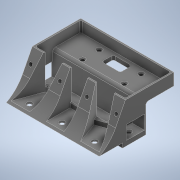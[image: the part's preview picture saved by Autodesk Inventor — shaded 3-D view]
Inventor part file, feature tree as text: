
AUTODESK INVENTOR PART (.ipt)
format: ipt  version: 2021 (Build 250183000, 183)  size: 572,928 bytes
history: native  units: mm
features: other x21, sketch x21, extrude x17, fillet x5, hole x5, chamfer x1
ambient origin geometry x8: Origin, YZ Plane, XZ Plane, XY Plane, X Axis, Y Axis, Z Axis, Center Point
bodies: Body1 (feature_tree)
feature tree (70):
  other  "Sólido1"
  extrude  "Extrusão1"  Depth=50.0mm
  extrude  "Extrusão2"  Depth=1.5mm
  extrude  "Extrusão3"  Depth=20.5mm
  other  "Plano de trabalho1"
  extrude  "Extrusão4"  TaperAngle=0.0deg  [1 undecoded]
  extrude  "Extrusão7"  Depth=1.5mm
  extrude  "Extrusão9"  Depth=50.0mm
  extrude  "Extrusão10"  Depth=1.5mm
  extrude  "Extrusão11"  Depth=25.0mm
  extrude  "Extrusão12"  Depth=5.0mm TaperAngle=0.0deg
  extrude  "Extrusão13"  Depth=19.0mm
  extrude  "Extrusão14"  Depth=1.5mm
  extrude  "Extrusão15"  TaperAngle=0.0deg  [1 undecoded]
  extrude  "Extrusão16"  Depth=14.5mm
  fillet  "Arredondamento2"  Radius=4.85mm
  fillet  "Arredondamento3"  Radius=1.5mm
  hole  "Furo1"  [1 undecoded]
  chamfer  "Chanfro1"  Distance=30.0mm
  extrude  "Extrusão17"  Depth=50.0mm
  fillet  "Arredondamento5"  Radius=2.85mm
  hole  "Furo2"  [1 undecoded]
  hole  "Furo3"  [1 undecoded]
  hole  "Furo4"  [1 undecoded]
  other  "Plano de trabalho2"
  hole  "Furo5"  [1 undecoded]
  extrude  "Extrusão18"  Depth=2.0mm TaperAngle=45.0deg
  extrude  "Extrusão19"  Depth=20.0mm
  fillet  "Arredondamento6"  Radius=12.5mm
  extrude  "Extrusão20"  Depth=50.0mm
  fillet  "Arredondamento7"  Radius=5.0mm
  sketch  "Esboço1"  dims[d0=38.5mm d1=50.0mm]
  sketch  "Esboço2"  dims[d2=100.0mm d3=0.0mm d4=1.5mm]
  other  "Contorno projetado1"
  sketch  "Esboço3"  dims[d5=20.5mm d6=4.886922mm]
  other  "Contorno projetado2"
  sketch  "Esboço4"  dims[d7=10.995574mm d8=0.0mm d9=0.0mm]
  other  "Contorno projetado3"
  other  "Contorno projetado4"
  other  "Contorno projetado5"
  sketch  "Esboço8"  dims[d12=37.0mm d13=0.0mm d14=1.5mm]
  other  "Contorno projetado8"
  sketch  "Esboço11"  dims[d15=19.0mm d16=50.0mm]
  other  "Contorno projetado9"
  sketch  "Esboço12"  dims[d17=19.0mm d19=1.5mm]
  sketch  "Esboço13"  dims[d20=0.0mm d21=0.0mm d32=25.0mm]
  sketch  "Esboço14"  dims[d33=4.85mm d34=0.0mm d37=5.0mm d38=0.0mm]
  sketch  "Esboço15"  dims[d39=4.85mm d40=0.0mm d41=19.0mm]
  sketch  "Esboço16"  dims[d42=15.0mm d43=1.5mm]
  sketch  "Esboço17"  dims[d44=5.0mm d45=0.0mm d46=0.0mm]
  other  "Contorno projetado10"
  sketch  "Esboço18"  dims[d47=14.5mm d48=14.5mm d49=4.85mm d50=0.0mm d51=1.5mm]
  sketch  "Esboço19"  dims[d52=1.5mm d53=4.85mm d54=0.0mm]
  sketch  "Esboço20"  dims[d55=13.0mm d56=30.0mm d57=0.0mm]
  sketch  "Esboço21"  dims[d58=55.0mm d59=50.0mm d60=2.85mm d61=0.0mm]
  sketch  "Esboço22"  dims[d62=1.5mm d63=11.5mm d64=0.0mm]
  other  "Contorno projetado11"
  other  "Contorno projetado12"
  sketch  "Esboço23"  dims[d66=2.85mm d67=1.5mm]
  other  "Contorno projetado13"
  other  "Contorno projetado14"
  other  "Contorno projetado15"
  other  "Contorno projetado16"
  sketch  "Esboço24"  dims[d69=4.5mm d70=5.0mm]
  other  "Contorno projetado17"
  other  "Contorno projetado18"
  sketch  "Esboço26"  dims[d71=5.0mm d72=7.5mm]
  other  "Contorno projetado19"
  other  "Contorno projetado20"
  sketch  "Esboço27"  dims[d73=4.0mm d74=6.0mm d75=4.0mm d76=2.0mm d77=90.0deg d78=5.0mm d79=0.0mm d80=1.0mm d81=2.0mm d82=45.0deg d83=20.0mm d84=12.5mm d85=50.0mm d86=5.0mm d87=0.0mm d88=0.0mm d89=2.0mm d90=8.0mm d91=50.0mm d92=10.0mm d95=4.0mm d96=6.0mm d97=6.0mm d98=2.0mm d99=90.0deg d100=8.0mm d101=20.594885mm d106=4.0mm d107=6.0mm d108=6.0mm d109=2.0mm d110=90.0deg d111=8.0mm d112=20.594885mm d113=4.0mm d114=6.0mm d115=6.0mm d116=2.0mm d117=90.0deg d118=8.0mm d119=20.594885mm d120=35.0mm d121=35.0mm d126=29.0mm d127=43.0mm d128=43.0mm d129=4.0mm d130=4.0mm d131=5.0mm d132=5.0mm d133=10.0mm d134=4.0mm d135=6.0mm d136=4.0mm d137=2.0mm d138=90.0deg d139=5.0mm d140=0.0mm d141=10.0mm d142=0.0mm d143=10.0mm d144=0.0mm d145=4.0mm d146=1.25mm d147=1.25mm d148=10.0mm d149=0.0mm d150=1.5mm]
note: 7 required parameter values undecoded (feature->parameter linkage not recoverable at this tier; creation-order binding heuristic only, values carry confidence <= 0.55)
